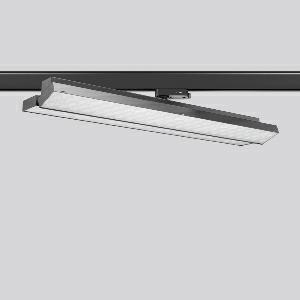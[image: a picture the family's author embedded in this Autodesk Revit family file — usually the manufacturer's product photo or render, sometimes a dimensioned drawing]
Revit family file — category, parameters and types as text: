
# Revit family: tx-move_742161_003_3_76_2676
name_source: partatom
category: Lighting Fixtures
units: mm (PartAtom-declared; Revit-internal decimal feet)

## family parameters
Cut with Voids When Loaded = No
Host = Face
Light Source = No
Part Type = Normal
Room Calculation Point = No
Round Connector Dimension = Use Diameter
Shared = No

## types (1)
- MultiLumen 1 (1 x LED Modul 835, 3025 lm, 3500)
    Apparent Load = 41 VA
    CIE Flux Codes = 88 96 99 100 100
    Color Rendering = 80
    Color Temperature = 3500
    Default Elevation = 1800 mm
    Description = Series: TX-MOVE
Multifunctional surface-mounted spotlight for area lighting. Very flat design. Housing: sheet steel, powder-coated. Rotation range: 356°. Swivel range: 90°. Consistent alignment possible with visible tilt scale. High-efficiency LED units with optimum light control thanks to clear plastic (PC) lens optics. Spezielle Mikrostrukturen reduzieren Gelbsaum. Symmetrical light distribution. With adapter for RZB 3-circuit DALI tracks. Suitable for Track on ceiling. MultiLumen: Luminous flux adjustable in 3 steps. Factory setting is the highest luminous flux. Environmentally friendly and resource-saving due to replaceable and recyclable components. 
Colour: deep black, matt (RAL 9005)
Length: 570 mm
Width: 119 mm
Height: 88 mm
Lamp: LED
Socket: without socket
Colour temperature: 3500K
Colour rendering index (CRI): 80
System power: 41 W
Rated luminous flux: 6050 lm
Luminous efficiency: 148 lm/W
System power 2: 57 W
Rated luminous flux 2: 8200 lm
Luminous efficiency 2: 144 lm/W
System power 3: 73 W
Rated luminous flux 3: 10000 lm
Luminous efficiency 3: 137 lm/W
Control gear: Dimmable EVG, DALI
Protection class: I
Type of protection: IP 20
    Height = 75 mm
    Lamp = 1 x LED Modul 835
    Lamp Light Flux = 3025 lm
    Lamp count = 1
    Length = 569 mm
    Lifetime = 50000 h
    Luminous efficacy = 148 lm/W
    Manufacturer = RZB
    ModVariant = No
    Model = 742161.003.3.76
    Mounting Place = Ceiling
    Mounting Type = Rail mounted
    Number of Poles = 1
    OnlyDefault = Yes
    Power Factor = 1
    Product Name = TX-MOVE
    Product group = Track mounted projectors
    ProductGroupID = 301
    Protection Class = Protection class I
    Protection Degree = IP 20
    RLX_Detail_Level = 1
    RLX_Emergency_Light_Flux = 0 lm
    RLX_Emergency_Type = 0
    RLX_Emergency_Type_DB = No
    RlxData = <blob elided: 36929 chars, md5=dc116672>
    Socket = socket
    Standby Power = 0 W
    System Light Flux = 6050 lm
    System Power = 41 W
    Type Comments = MultiLumen 1
    Type Image = 742162.003.jpg
    URL = http://relux.com
    VarID = multilumen_1
    Voltage = 230 V
    Voltage Range = 220-240 V
    Weight = 0.00 kg
    Width = 119 mm

## geometry (parser evidence)
native form markers: Blend x4, Sweep x13
no freeform markers — native parametric forms only
